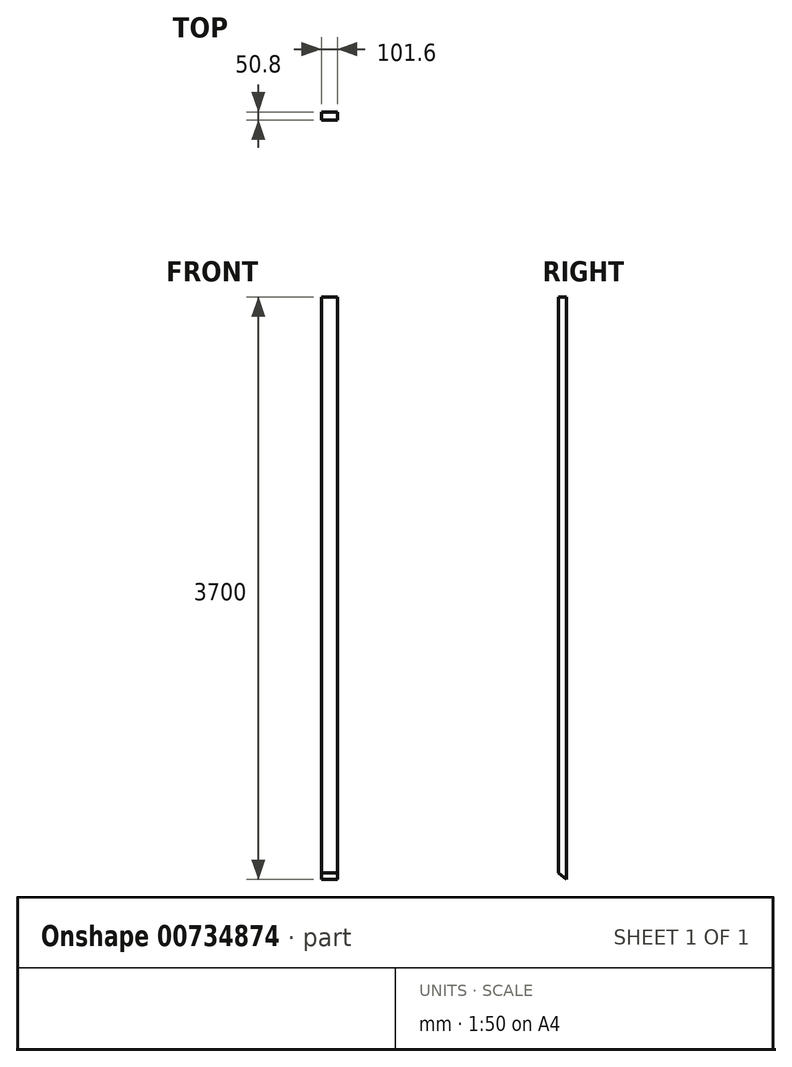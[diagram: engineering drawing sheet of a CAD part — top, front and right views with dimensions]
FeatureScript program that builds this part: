
annotation { "Feature Type Name" : "Feature", "Feature Type Description" : "" }
export const myFeature = defineFeature(function(context is Context, id is Id, definition is map)
    precondition{}
    {
        {
            var Q0;
            Q0=qCreatedBy(makeId("Top.planeOp"),FACE);
            var sketch = newSketch(context, id + "F0", { "sketchPlane" : qUnion([Q0])});
            skLineSegment(sketch, "E0.bottom", {"start": v(50.8, -25.4) * mm, "end": v(-50.8, -25.4) * mm});
            skLineSegment(sketch, "E0.top", {"start": v(50.8, 25.4) * mm, "end": v(-50.8, 25.4) * mm});
            skLineSegment(sketch, "E0.left", {"start": v(50.8, -25.4) * mm, "end": v(50.8, 25.4) * mm});
            skLineSegment(sketch, "E0.right", {"start": v(-50.8, -25.4) * mm, "end": v(-50.8, 25.4) * mm});
            skPoint(sketch, "E0.middle", {"position": v(0, 0) * mm});
            skSolve(sketch);
        }
        {
            var Q0;
            Q0=makeQuery(id+"F0.imprint","IMPRINT",FACE,{"disambiguationData":[TD([[makeQuery(id+"F0.imprint","IMPRINT",EDGE,{"derivedFrom":sQuery(id+"F0.wireOp",EDGE,"E0.bottom")}),-1.0]])]});
            extrude(context, id + "F1", {"entities" : qUnion([Q0]), "endBound" : BoundingType.SYMMETRIC, "depth" : 3700 * mm, "offsetDistance" : 25.4 * mm});
        }
        {
            var Q0;
            Q0=makeQuery(id+"F1.opExtrude","SWEPT_FACE",FACE,{"disambiguationData":[OSD([sQuery(id+"F0.wireOp",EDGE,"E0.left")])]});
            var sketch = newSketch(context, id + "F2", { "sketchPlane" : qUnion([Q0])});
            skLineSegment(sketch, "E1", {"start": v(25.4, -1850) * mm, "end": v(-25.4, -1807.37) * mm});
            skLineSegment(sketch, "E2", {"start": v(-25.4, -1807.37) * mm, "end": v(-79.6, -1807.37) * mm});
            skLineSegment(sketch, "E3", {"start": v(-79.6, -1807.37) * mm, "end": v(-79.6, -1880.03) * mm});
            skLineSegment(sketch, "E4", {"start": v(-79.6, -1880.03) * mm, "end": v(25.4, -1880.03) * mm});
            skLineSegment(sketch, "E5", {"start": v(25.4, -1880.03) * mm, "end": v(25.4, -1850) * mm});
            skSolve(sketch);
        }
        {
            var Q0;
            {var subQ0=sQuery(id+"F2.wireOp",EDGE,"E2");Q0=makeQuery(id+"F2.imprint","IMPRINT",FACE,{"disambiguationData":[TD([[makeQuery(id+"F2.imprint","IMPRINT",EDGE,{"derivedFrom":subQ0}),1.0]])]});}
            var Q1;
            {var subQ0=sQuery(id+"F2.wireOp",EDGE,"E1");Q1=makeQuery(id+"F2.imprint","IMPRINT",FACE,{"disambiguationData":[TD([[makeQuery(id+"F2.imprint","IMPRINT",EDGE,{"derivedFrom":subQ0}),1.0]])]});}
            extrude(context, id + "F3", {"entities" : qUnion([Q0, Q1]), "operationType" : NewBodyOperationType.REMOVE, "endBound" : BoundingType.THROUGH_ALL, "oppositeDirection" : true, "depth" : 25.4 * mm, "offsetDistance" : 25.4 * mm});
        }
    });
